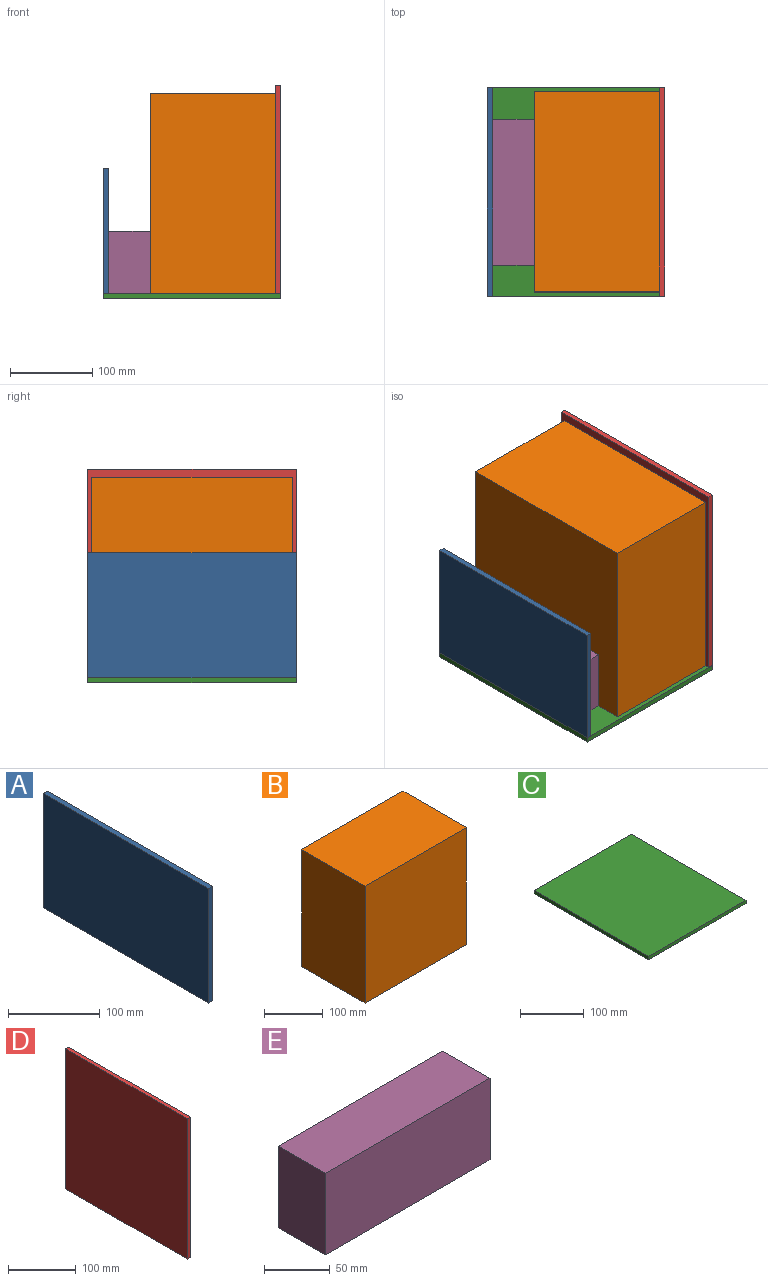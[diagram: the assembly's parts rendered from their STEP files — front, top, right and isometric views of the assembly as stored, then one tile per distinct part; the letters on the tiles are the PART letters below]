
ASSEMBLY  parts=5 mates=4
PART A: 6 faces, bbox 6.4x254x152.4 mm
  f0: plane 254x6.35mm, normal (0,0,-1), area 1612.9mm2, adj f1,f3,f4,f5
  f1: plane 152.4x6.35mm, normal (0,1,0), area 967.7mm2, adj f0,f2,f4,f5
  f2: plane 254x6.35mm, normal (0,0,1), area 1612.9mm2, adj f1,f3,f4,f5
  f3: plane 152.4x6.35mm, normal (0,-1,0), area 967.7mm2, adj f0,f2,f4,f5
  f4: plane 254x152.4mm, normal (1,0,0), area 38709.6mm2, adj f0,f1,f2,f3
  f5: plane 254x152.4mm, normal (-1,0,0), area 38709.6mm2, adj f0,f1,f2,f3
PART B: 6 faces, bbox 243.8x152.4x243.8 mm
  f0: plane 243.84x152.4mm, normal (0,0,-1), area 37161.2mm2, adj f1,f3,f4,f5
  f1: plane 243.84x152.4mm, normal (1,0,0), area 37161.2mm2, adj f0,f2,f4,f5
  f2: plane 243.84x152.4mm, normal (0,0,1), area 37161.2mm2, adj f1,f3,f4,f5
  f3: plane 243.84x152.4mm, normal (-1,0,0), area 37161.2mm2, adj f0,f2,f4,f5
  f4: plane 243.84x243.84mm, normal (0,-1,0), area 59457.9mm2, adj f0,f1,f2,f3
  f5: plane 243.84x243.84mm, normal (0,1,0), area 59457.9mm2, adj f0,f1,f2,f3
PART C: 6 faces, bbox 215.9x254x6.4 mm
  f0: plane 215.9x6.35mm, normal (0,-1,0), area 1371mm2, adj f1,f3,f4,f5
  f1: plane 254x6.35mm, normal (1,0,0), area 1612.9mm2, adj f0,f2,f4,f5
  f2: plane 215.9x6.35mm, normal (0,1,0), area 1371mm2, adj f1,f3,f4,f5
  f3: plane 254x6.35mm, normal (-1,0,0), area 1612.9mm2, adj f0,f2,f4,f5
  f4: plane 254x215.9mm, normal (0,0,1), area 54838.6mm2, adj f0,f1,f2,f3
  f5: plane 254x215.9mm, normal (0,0,-1), area 54838.6mm2, adj f0,f1,f2,f3
PART D: 6 faces, bbox 6.4x254x254 mm
  f0: plane 254x6.35mm, normal (0,0,-1), area 1612.9mm2, adj f1,f3,f4,f5
  f1: plane 254x6.35mm, normal (0,1,0), area 1612.9mm2, adj f0,f2,f4,f5
  f2: plane 254x6.35mm, normal (0,0,1), area 1612.9mm2, adj f1,f3,f4,f5
  f3: plane 254x6.35mm, normal (0,-1,0), area 1612.9mm2, adj f0,f2,f4,f5
  f4: plane 254x254mm, normal (1,0,0), area 64516mm2, adj f0,f1,f2,f3
  f5: plane 254x254mm, normal (-1,0,0), area 64516mm2, adj f0,f1,f2,f3
PART E: 11 faces, bbox 177.8x50.8x76.2 mm
  f0: plane 76.2x50.8mm, normal (1,0,0), area 3152.5mm2, adj f1,f2,f4,f5,f6,f7,f8,f9
  f1: plane 177.8x76.2mm, normal (0,-1,0), area 13548.4mm2, adj f0,f3,f4,f5
  f2: plane 177.8x76.2mm, normal (0,1,0), area 13548.4mm2, adj f0,f3,f4,f5
  f3: plane 76.2x50.8mm, normal (-1,0,0), area 3871mm2, adj f1,f2,f4,f5
  f4: plane 177.8x50.8mm, normal (0,0,1), area 9032.2mm2, adj f0,f1,f2,f3
  f5: plane 177.8x50.8mm, normal (0,0,-1), area 9032.2mm2, adj f0,f1,f2,f3
  f6: plane 31.64x7.62mm, normal (0,1,0), area 241.1mm2, adj f0,f7,f9,f10
  f7: plane 22.71x7.62mm, normal (0,0,1), area 173mm2, adj f0,f6,f8,f10
  f8: plane 31.64x7.62mm, normal (0,-1,0), area 241.1mm2, adj f0,f7,f9,f10
  f9: plane 22.71x7.62mm, normal (0,0,-1), area 173mm2, adj f0,f6,f8,f10
  f10: plane 31.64x22.71mm, normal (1,0,0), area 718.4mm2, adj f6,f7,f8,f9
PLACE A rot(axis=(0,0,1),180deg) t=(-203.2,5.04,-50.8)mm
PLACE B rot(axis=(0,0,-1),90deg) t=(0,5.04,-5.08)mm
PLACE C t=(-101.6,5.04,-133.35)mm
PLACE D at identity
PLACE E rot(axis=(0,0,1),90deg) t=(-177.8,5.04,-127)mm
MATE fastened C.f4 <-> D.f0  axis (0,0,1) through (6.35,5.04,-127)mm
MATE fastened E.f1 <-> B.f4  axis (1,0,0) through (-152.4,5.04,-127)mm
MATE fastened B.f5 <-> D.f5  axis (1,0,0) through (0,5.04,-127)mm
MATE fastened A.f5 <-> E.f2  axis (1,0,0) through (-203.2,5.04,-127)mm
